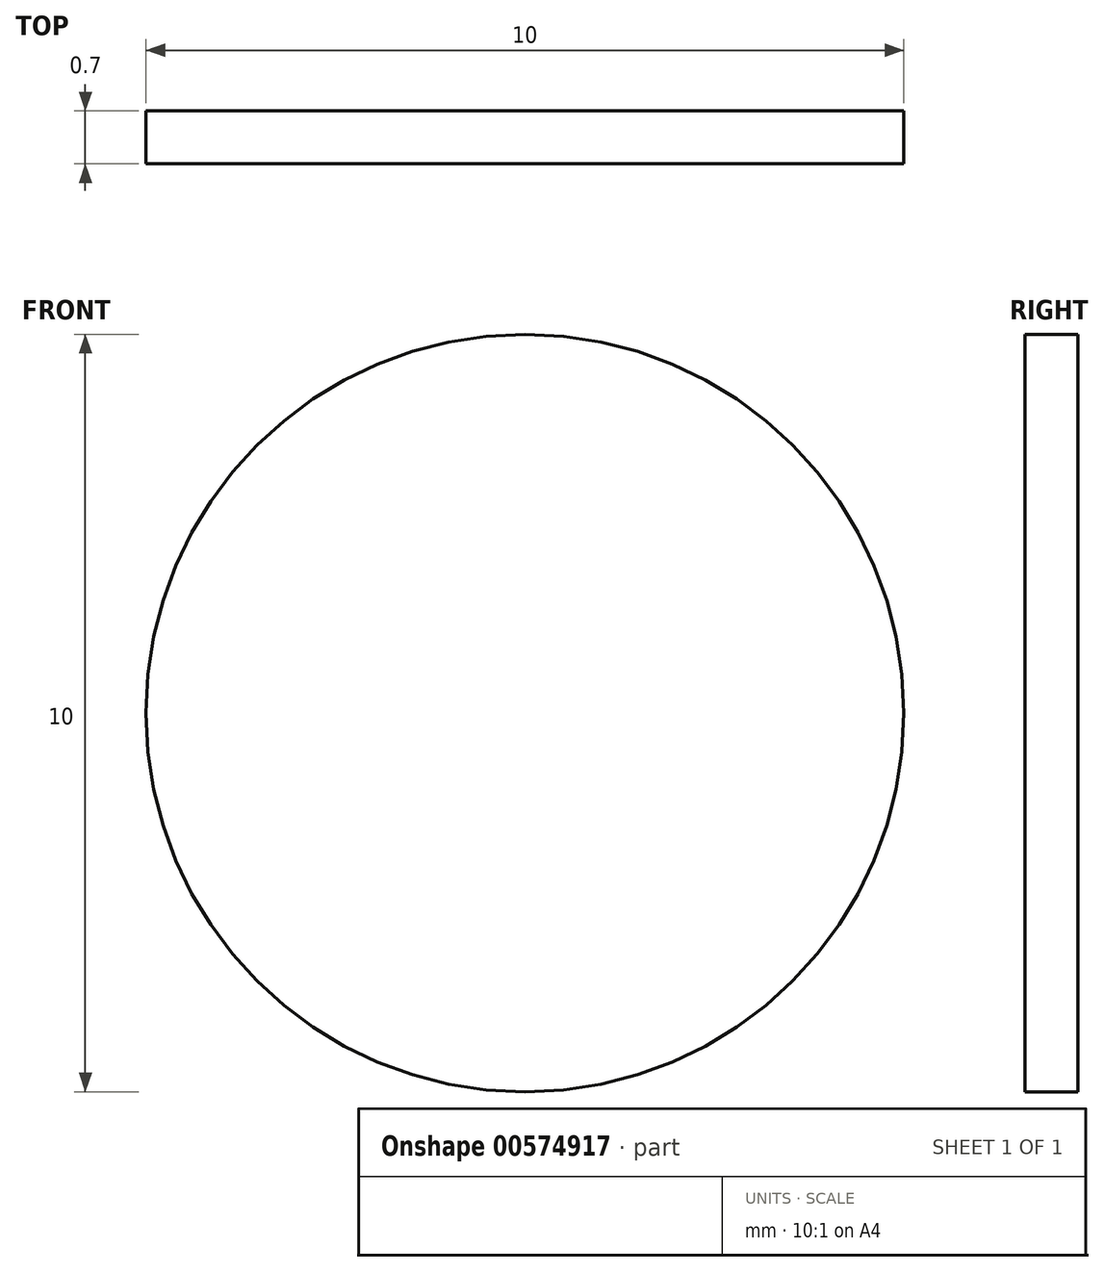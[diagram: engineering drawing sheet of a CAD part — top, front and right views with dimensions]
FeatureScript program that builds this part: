
annotation { "Feature Type Name" : "Feature", "Feature Type Description" : "" }
export const myFeature = defineFeature(function(context is Context, id is Id, definition is map)
    precondition{}
    {
        {
            var Q0;
            Q0=qCreatedBy(makeId("Front.planeOp"),FACE);
            var sketch = newSketch(context, id + "F0", { "sketchPlane" : qUnion([Q0])});
            skCircle(sketch, "E0", {"center": v(0, 0) * mm, "radius": 5 * mm});
            skSolve(sketch);
        }
        {
            var Q0;
            Q0=makeQuery(id+"F0.imprint","IMPRINT",FACE,{"disambiguationData":[TD([[makeQuery(id+"F0.imprint","IMPRINT",EDGE,{"derivedFrom":sQuery(id+"F0.wireOp",EDGE,"E0")}),1.0]])]});
            extrude(context, id + "F1", {"entities" : qUnion([Q0]), "depth" : 0.7 * mm, "offsetDistance" : 25 * mm});
        }
    });
